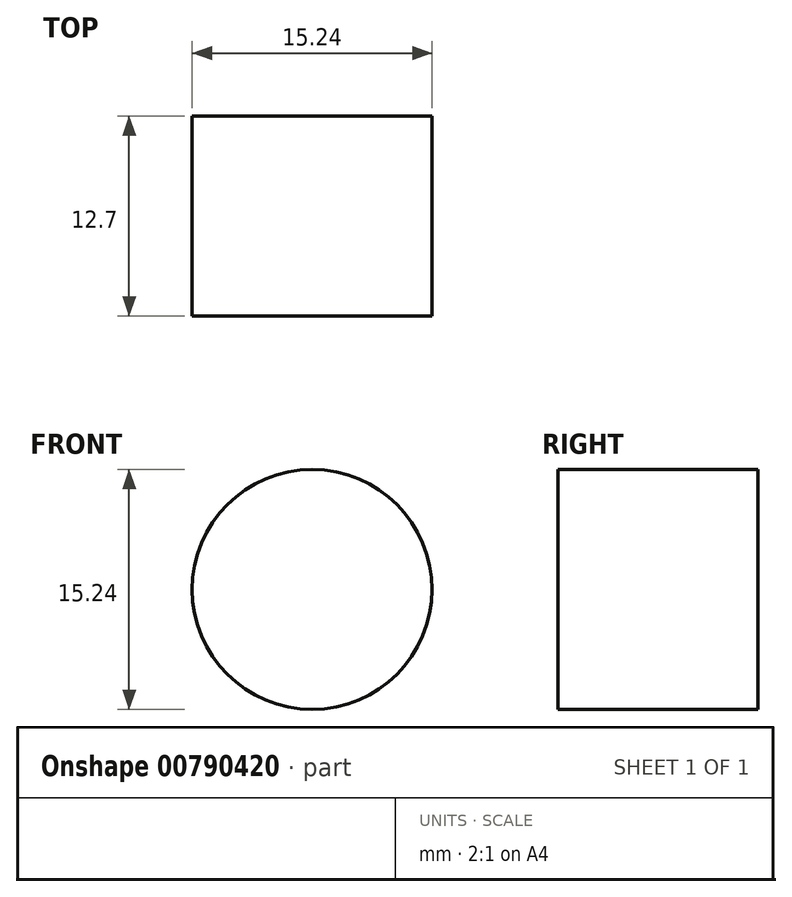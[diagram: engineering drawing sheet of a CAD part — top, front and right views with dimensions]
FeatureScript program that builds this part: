
annotation { "Feature Type Name" : "Feature", "Feature Type Description" : "" }
export const myFeature = defineFeature(function(context is Context, id is Id, definition is map)
    precondition{}
    {
        {
            var Q0;
            Q0=qCreatedBy(makeId("Front.planeOp"),FACE);
            var sketch = newSketch(context, id + "F0", { "sketchPlane" : qUnion([Q0])});
            skCircle(sketch, "E0", {"center": v(0, 0) * mm, "radius": 7.62 * mm});
            skSolve(sketch);
        }
        {
            var Q0;
            Q0=makeQuery(id+"F0.imprint","IMPRINT",FACE,{"disambiguationData":[TD([[makeQuery(id+"F0.imprint","IMPRINT",EDGE,{"derivedFrom":sQuery(id+"F0.wireOp",EDGE,"E0")}),1.0]])]});
            extrude(context, id + "F1", {"entities" : qUnion([Q0]), "depth" : 12.7 * mm, "offsetDistance" : 25.4 * mm});
        }
    });
